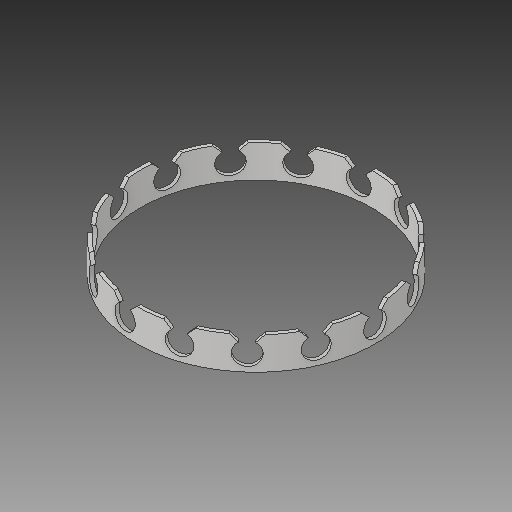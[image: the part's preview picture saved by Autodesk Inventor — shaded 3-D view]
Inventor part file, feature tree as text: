
AUTODESK INVENTOR PART (.ipt)
format: ipt  version: 2018 (Build 220112000, 112)  size: 265,728 bytes
history: native  units: in
note: dims shown in document units (in); Inventor stores cm internally (conversion verified against a paired STEP export)
features: extrude x3, sketch x3, mirror x1, pattern_circular x1
ambient origin geometry x8: Origin, YZ Plane, XZ Plane, XY Plane, X Axis, Y Axis, Z Axis, Center Point
bodies: Solid1 (feature_tree)
feature tree (8):
  extrude  "Extrusion1"  Depth=3.57in
  extrude  "Extrusion2"  Depth=0.3in
  sketch  "Sketch3"  dims[d5=0.25in d6=3.0625in d7=0.0in d8=0.35in d9=0.25in d11=45.0deg d14=0.0938in d17=5.9055in d18=360.0deg d21=0.08in d25=3.0625in d26=0.0in]
  extrude  "Extrusion5"  Depth=0.25in TaperAngle=0.0deg
  mirror  "Mirror3"
  pattern_circular  "Circular Pattern1"  [2 undecoded]
  sketch  "Sketch1"  dims[d0=3.68in d1=3.57in]
  sketch  "Sketch2"  dims[d2=0.5in d3=0.0in d4=0.3in]
note: 2 required parameter values undecoded (feature->parameter linkage not recoverable at this tier; creation-order binding heuristic only, values carry confidence <= 0.55)
